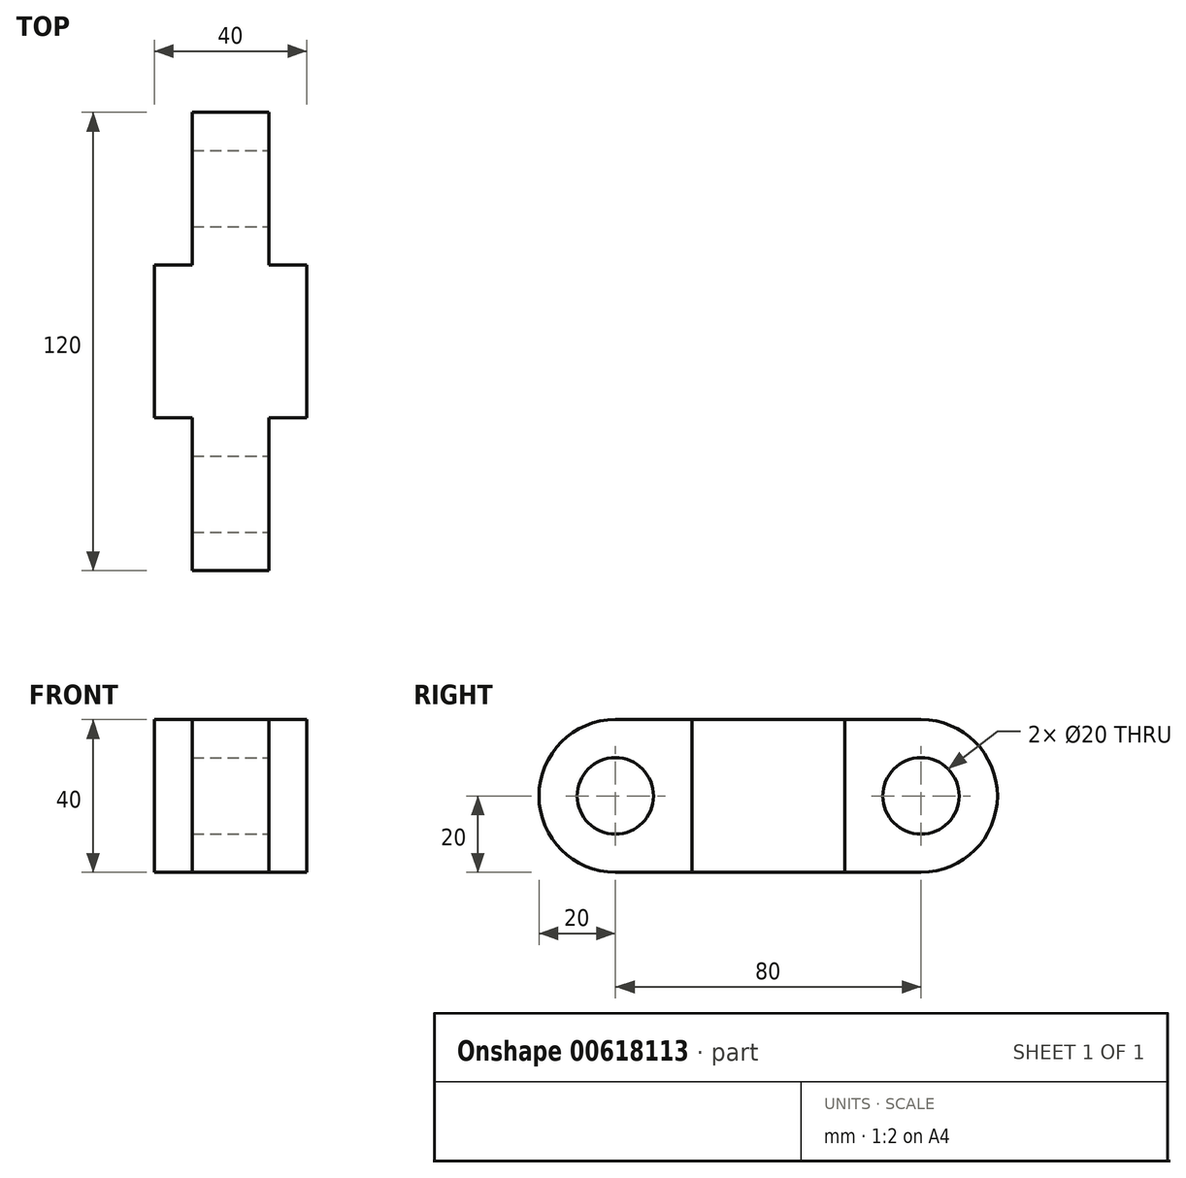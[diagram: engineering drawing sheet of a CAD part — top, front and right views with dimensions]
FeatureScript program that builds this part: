
annotation { "Feature Type Name" : "Feature", "Feature Type Description" : "" }
export const myFeature = defineFeature(function(context is Context, id is Id, definition is map)
    precondition{}
    {
        {
            var Q0;
            Q0=qCreatedBy(makeId("Top.planeOp"),FACE);
            var sketch = newSketch(context, id + "F0", { "sketchPlane" : qUnion([Q0])});
            skLineSegment(sketch, "E0", {"start": v(0, 120) * mm, "end": v(-10, 120) * mm});
            skLineSegment(sketch, "E1", {"start": v(-10, 120) * mm, "end": v(-10, 80) * mm});
            skLineSegment(sketch, "E2", {"start": v(-10, 80) * mm, "end": v(-20, 80) * mm});
            skLineSegment(sketch, "E3", {"start": v(-20, 80) * mm, "end": v(-20, 40) * mm});
            skLineSegment(sketch, "E4", {"start": v(-20, 40) * mm, "end": v(-10, 40) * mm});
            skLineSegment(sketch, "E5", {"start": v(-10, 40) * mm, "end": v(-10, 0) * mm});
            skLineSegment(sketch, "E6", {"start": v(-10, 0) * mm, "end": v(0, 0) * mm});
            skLineSegment(sketch, "E7", {"start": v(0, 0) * mm, "end": v(0, 120) * mm});
            skLineSegment(sketch, "E8.MirrorCS", {"start": v(10, 120) * mm, "end": v(10, 80) * mm});
            skLineSegment(sketch, "E9.MirrorCS", {"start": v(0, 120) * mm, "end": v(10, 120) * mm});
            skLineSegment(sketch, "E10.MirrorCS", {"start": v(10, 80) * mm, "end": v(20, 80) * mm});
            skLineSegment(sketch, "E11.MirrorCS", {"start": v(20, 80) * mm, "end": v(20, 40) * mm});
            skLineSegment(sketch, "E12.MirrorCS", {"start": v(10, 40) * mm, "end": v(10, 0) * mm});
            skLineSegment(sketch, "E13.MirrorCS", {"start": v(20, 40) * mm, "end": v(10, 40) * mm});
            skLineSegment(sketch, "E14.MirrorCS", {"start": v(10, 0) * mm, "end": v(0, 0) * mm});
            skSolve(sketch);
        }
        {
            var Q0;
            Q0 = qSketchRegion(id + "F0", true);
            extrude(context, id + "F1", {"entities" : qUnion([Q0]), "depth" : 40 * mm, "offsetDistance" : 25 * mm});
        }
        {
            var Q0;
            Q0=makeQuery(id+"F1.opExtrude","SWEPT_FACE",FACE,{"disambiguationData":[OSD([sQuery(id+"F0.wireOp",EDGE,"E12.MirrorCS")])]});
            var sketch = newSketch(context, id + "F2", { "sketchPlane" : qUnion([Q0])});
            skCircle(sketch, "E15", {"center": v(20, 20) * mm, "radius": 10 * mm});
            skPoint(sketch, "E15.centerSnap0", {"position": v(20, 40) * mm});
            skPoint(sketch, "E15.centerSnap1", {"position": v(40, 20) * mm});
            skSolve(sketch);
        }
        {
            var Q0;
            Q0 = qSketchRegion(id + "F2", true);
            extrude(context, id + "F3", {"entities" : qUnion([Q0]), "operationType" : NewBodyOperationType.REMOVE, "endBound" : BoundingType.UP_TO_NEXT, "oppositeDirection" : true, "depth" : 20 * mm, "offsetDistance" : 25 * mm});
        }
        {
            var Q0;
            Q0=makeQuery(id+"F1.opExtrude","SWEPT_FACE",FACE,{"disambiguationData":[OSD([sQuery(id+"F0.wireOp",EDGE,"E8.MirrorCS")])]});
            var sketch = newSketch(context, id + "F4", { "sketchPlane" : qUnion([Q0])});
            skCircle(sketch, "E16", {"center": v(100, 20) * mm, "radius": 10 * mm});
            skPoint(sketch, "E16.centerSnap0", {"position": v(100, 40) * mm});
            skPoint(sketch, "E16.centerSnap1", {"position": v(120, 20) * mm});
            skSolve(sketch);
        }
        {
            var Q0;
            Q0 = qSketchRegion(id + "F4", true);
            extrude(context, id + "F5", {"entities" : qUnion([Q0]), "operationType" : NewBodyOperationType.REMOVE, "endBound" : BoundingType.UP_TO_NEXT, "oppositeDirection" : true, "depth" : 25 * mm, "offsetDistance" : 25 * mm});
        }
        {
            var Q0;
            Q0=makeQuery(id+"F1.opExtrude","CAP_EDGE",EDGE,{"disambiguationData":[OSD([sQuery(id+"F0.wireOp",EDGE,"E0"),sQuery(id+"F0.wireOp",EDGE,"E9.MirrorCS")])],"isStart":true});
            var Q1;
            Q1=makeQuery(id+"F1.opExtrude","CAP_EDGE",EDGE,{"disambiguationData":[OSD([sQuery(id+"F0.wireOp",EDGE,"E0"),sQuery(id+"F0.wireOp",EDGE,"E9.MirrorCS")])],"isStart":false});
            fillet(context, id + "F6", {"entities" : qUnion([Q0, Q1]), "radius" : 20 * mm, "tangentPropagation" : true, "allowEdgeOverflow" : false});
        }
        {
            var Q0;
            Q0=makeQuery(id+"F1.opExtrude","CAP_EDGE",EDGE,{"disambiguationData":[OSD([sQuery(id+"F0.wireOp",EDGE,"E6"),sQuery(id+"F0.wireOp",EDGE,"E14.MirrorCS")])],"isStart":false});
            var Q1;
            Q1=makeQuery(id+"F1.opExtrude","CAP_EDGE",EDGE,{"disambiguationData":[OSD([sQuery(id+"F0.wireOp",EDGE,"E6"),sQuery(id+"F0.wireOp",EDGE,"E14.MirrorCS")])],"isStart":true});
            fillet(context, id + "F7", {"entities" : qUnion([Q0, Q1]), "radius" : 20 * mm, "tangentPropagation" : true, "allowEdgeOverflow" : false});
        }
    });
